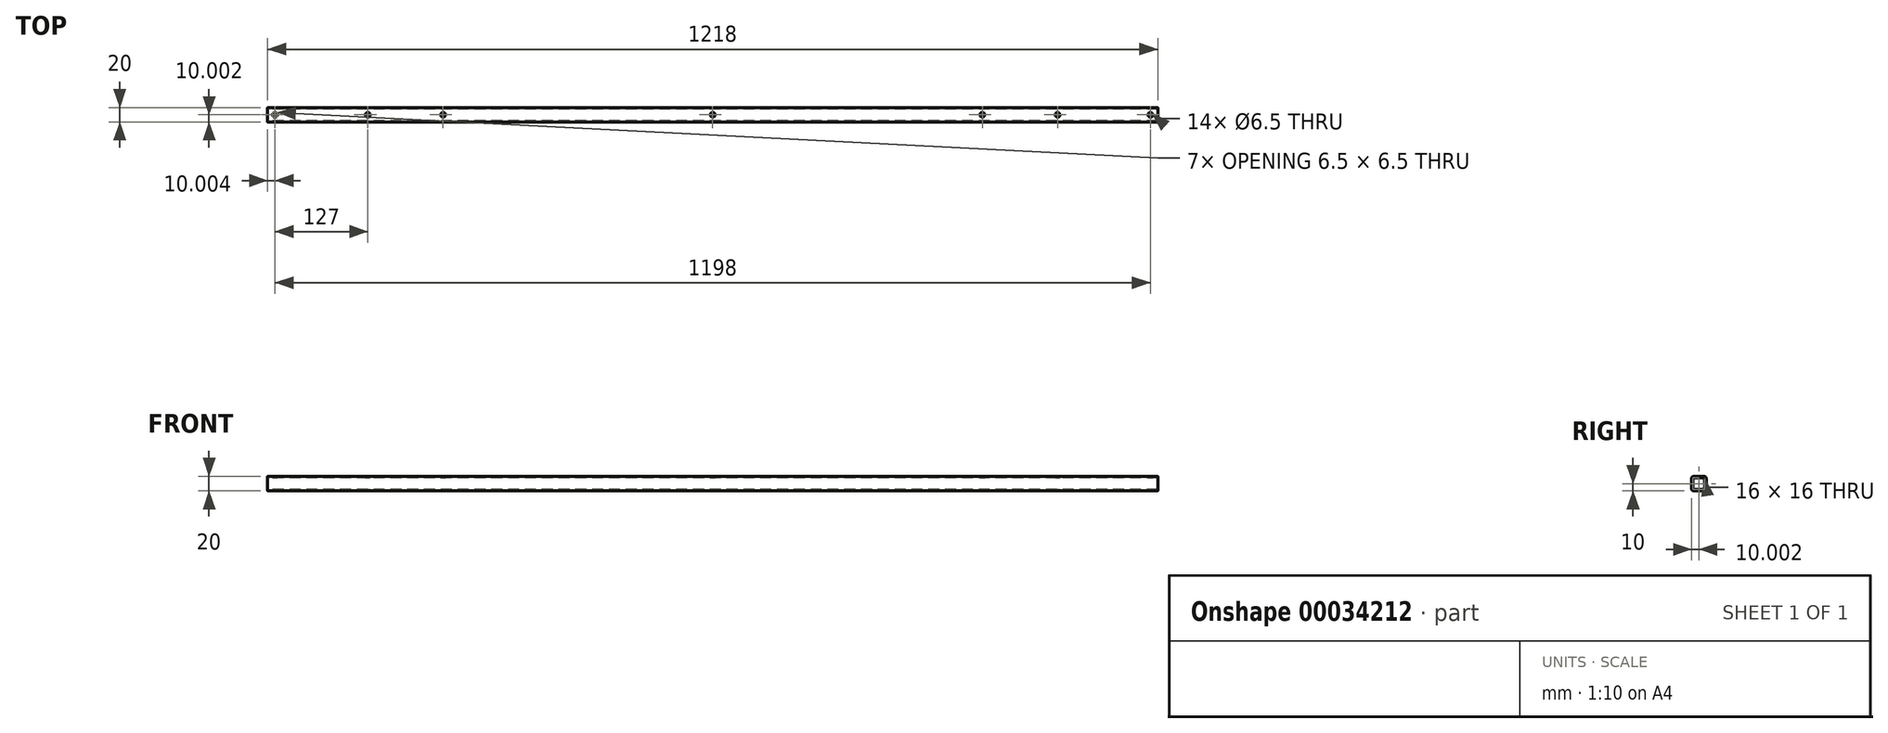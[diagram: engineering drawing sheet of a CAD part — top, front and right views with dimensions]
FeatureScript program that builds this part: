
annotation { "Feature Type Name" : "Feature", "Feature Type Description" : "" }
export const myFeature = defineFeature(function(context is Context, id is Id, definition is map)
    precondition{}
    {
        {
            var Q0;
            Q0=qCreatedBy(makeId("Top.planeOp"),FACE);
            var sketch = newSketch(context, id + "F0", { "sketchPlane" : qUnion([Q0])});
            skLineSegment(sketch, "E0.bottom", {"start": v(-658.22, -111.7) * mm, "end": v(559.78, -111.7) * mm});
            skLineSegment(sketch, "E0.top", {"start": v(-658.22, -131.7) * mm, "end": v(559.78, -131.7) * mm});
            skLineSegment(sketch, "E0.left", {"start": v(-658.22, -111.7) * mm, "end": v(-658.22, -131.7) * mm});
            skLineSegment(sketch, "E0.right", {"start": v(559.78, -111.7) * mm, "end": v(559.78, -131.7) * mm});
            skLineSegment(sketch, "E1.bottom", {"start": v(559.78, -111.7) * mm, "end": v(549.78, -111.7) * mm});
            skLineSegment(sketch, "E1.left", {"start": v(559.78, -111.7) * mm, "end": v(559.78, -121.7) * mm});
            skCircle(sketch, "E2", {"center": v(549.78, -121.7) * mm, "radius": 3.25 * mm});
            skCircle(sketch, "E3", {"center": v(-49.22, -121.7) * mm, "radius": 3.25 * mm});
            skLineSegment(sketch, "E4.bottom", {"start": v(-49.22, -131.7) * mm, "end": v(422.78, -131.7) * mm});
            skCircle(sketch, "E5", {"center": v(422.78, -121.7) * mm, "radius": 3.25 * mm});
            skLineSegment(sketch, "E6.bottom", {"start": v(559.78, -131.7) * mm, "end": v(319.78, -131.7) * mm});
            skLineSegment(sketch, "E6.left", {"start": v(559.78, -131.7) * mm, "end": v(559.78, -121.7) * mm});
            skCircle(sketch, "E7", {"center": v(319.78, -121.7) * mm, "radius": 3.25 * mm});
            skCircle(sketch, "E8.MirrorC", {"center": v(-418.22, -121.7) * mm, "radius": 3.25 * mm});
            skCircle(sketch, "E9.MirrorC", {"center": v(-648.22, -121.7) * mm, "radius": 3.25 * mm});
            skCircle(sketch, "E10.MirrorC", {"center": v(-521.22, -121.7) * mm, "radius": 3.25 * mm});
            skPoint(sketch, "E11.start.orphan", {"position": v(-49.22, -111.7) * mm});
            skSolve(sketch);
        }
        {
            var Q0;
            Q0=makeQuery(id+"F0.imprint","IMPRINT",FACE,{"disambiguationData":[TD([[makeQuery(id+"F0.imprint","IMPRINT",EDGE,{"derivedFrom":sQuery(id+"F0.wireOp",EDGE,"E0.bottom")}),-1.0]])]});
            extrude(context, id + "F1", {"entities" : qUnion([Q0]), "depth" : 20 * mm});
        }
        {
            var Q0;
            Q0=makeQuery(id+"F1.opExtrude","SWEPT_FACE",FACE,{"disambiguationData":[OSD([sQuery(id+"F0.wireOp",EDGE,"E0.left")])]});
            var sketch = newSketch(context, id + "F2", { "sketchPlane" : qUnion([Q0])});
            skLineSegment(sketch, "E12.rect.bottom", {"start": v(113.7, 2) * mm, "end": v(129.7, 2) * mm});
            skLineSegment(sketch, "E12.rect.top", {"start": v(113.7, 18) * mm, "end": v(129.7, 18) * mm});
            skLineSegment(sketch, "E12.rect.left", {"start": v(113.7, 2) * mm, "end": v(113.7, 18) * mm});
            skLineSegment(sketch, "E12.rect.right", {"start": v(129.7, 2) * mm, "end": v(129.7, 18) * mm});
            skPoint(sketch, "E12.rect.middle", {"position": v(121.7, 10) * mm});
            skPoint(sketch, "E12.rect.middle.positionSnap0", {"position": v(111.7, 10) * mm});
            skPoint(sketch, "E12.rect.middle.positionSnap1", {"position": v(121.7, 0) * mm});
            skPoint(sketch, "E12.rect.centerSnap0", {"position": v(111.7, 10) * mm});
            skPoint(sketch, "E12.rect.centerSnap1", {"position": v(121.7, 0) * mm});
            skSolve(sketch);
        }
        {
            var Q0;
            Q0=makeQuery(id+"F2.imprint","IMPRINT",FACE,{"disambiguationData":[TD([[makeQuery(id+"F2.imprint","IMPRINT",EDGE,{"derivedFrom":sQuery(id+"F2.wireOp",EDGE,"E12.rect.bottom")}),1.0]])]});
            extrude(context, id + "F3", {"entities" : qUnion([Q0]), "operationType" : NewBodyOperationType.REMOVE, "oppositeDirection" : true, "depth" : 1220 * mm});
        }
        {
            var Q0;
            Q0=makeQuery(id+"F1.opExtrude","CAP_EDGE",EDGE,{"disambiguationData":[OSD([sQuery(id+"F0.wireOp",EDGE,"E0.top"),sQuery(id+"F0.wireOp",EDGE,"E4.bottom"),sQuery(id+"F0.wireOp",EDGE,"E6.bottom")])],"isStart":false});
            var Q1;
            Q1=makeQuery(id+"F1.opExtrude","CAP_EDGE",EDGE,{"disambiguationData":[OSD([sQuery(id+"F0.wireOp",EDGE,"E0.bottom"),sQuery(id+"F0.wireOp",EDGE,"E1.bottom")])],"isStart":false});
            var Q2;
            Q2=makeQuery(id+"F1.opExtrude","CAP_EDGE",EDGE,{"disambiguationData":[OSD([sQuery(id+"F0.wireOp",EDGE,"E0.top"),sQuery(id+"F0.wireOp",EDGE,"E4.bottom"),sQuery(id+"F0.wireOp",EDGE,"E6.bottom")])],"isStart":true});
            var Q3;
            Q3=makeQuery(id+"F1.opExtrude","CAP_EDGE",EDGE,{"disambiguationData":[OSD([sQuery(id+"F0.wireOp",EDGE,"E0.bottom"),sQuery(id+"F0.wireOp",EDGE,"E1.bottom")])],"isStart":true});
            fillet(context, id + "F4", {"entities" : qUnion([Q0, Q1, Q2, Q3]), "radius" : 3 * mm, "tangentPropagation" : true, "allowEdgeOverflow" : false});
        }
    });
